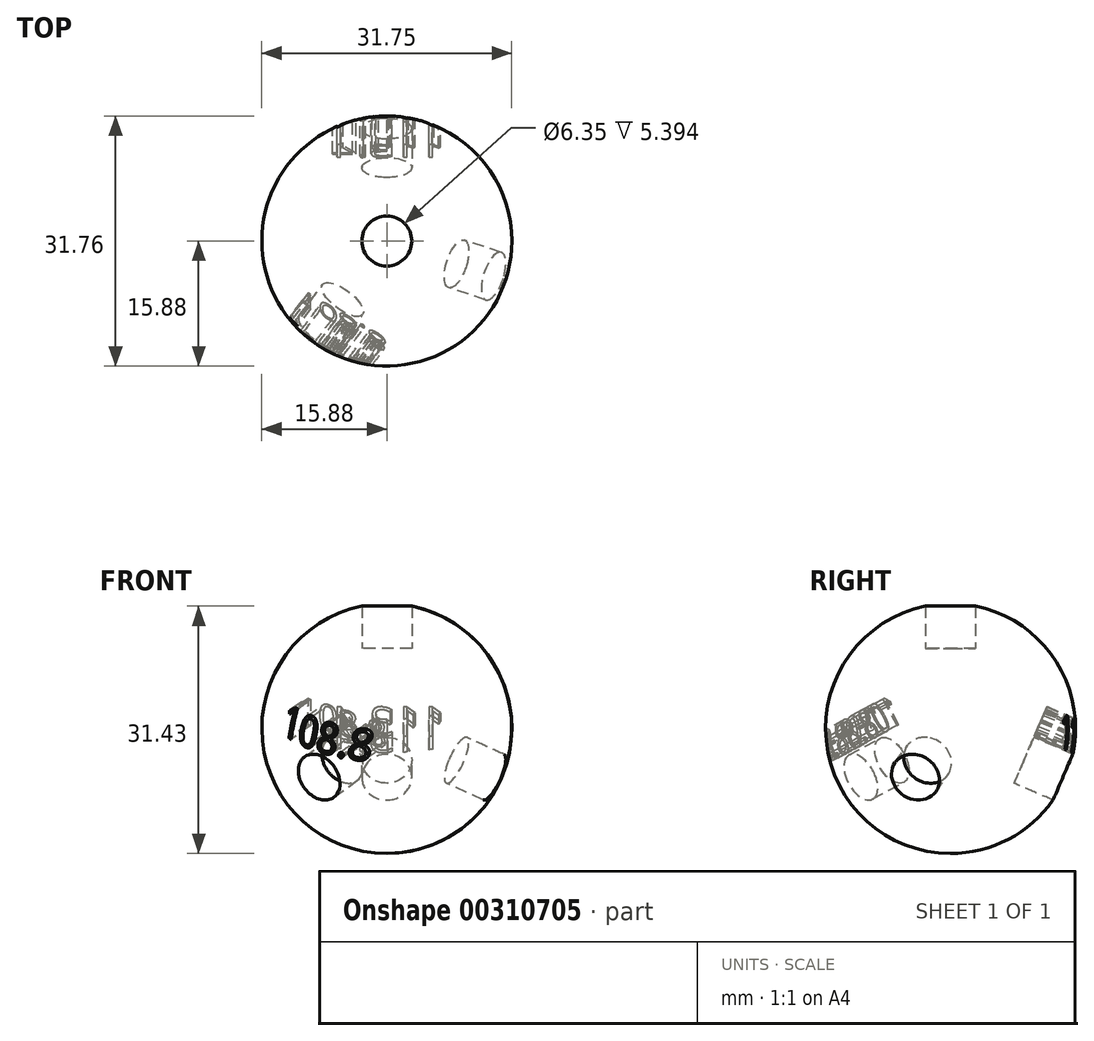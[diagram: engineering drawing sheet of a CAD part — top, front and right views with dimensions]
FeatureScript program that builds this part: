
annotation { "Feature Type Name" : "Feature", "Feature Type Description" : "" }
export const myFeature = defineFeature(function(context is Context, id is Id, definition is map)
    precondition{}
    {
        {
            var Q0;
            Q0=qCreatedBy(makeId("Front.planeOp"),FACE);
            var sketch = newSketch(context, id + "F0", { "sketchPlane" : qUnion([Q0])});
            skArc(sketch, "E0", {"start": v(0, 15.88) * mm, "mid": v(-15.88, 0) * mm, "end": v(0, -15.88) * mm});
            skLineSegment(sketch, "E1", {"start": v(0, 15.88) * mm, "end": v(0, -15.88) * mm});
            skSolve(sketch);
        }
        {
            var Q0;
            Q0=qCreatedBy(makeId("Top.planeOp"),FACE);
            var sketch = newSketch(context, id + "F1", { "sketchPlane" : qUnion([Q0])});
            skCircle(sketch, "E2", {"center": v(0, 0) * mm, "radius": 15.88 * mm});
            skSolve(sketch);
        }
        {
            var Q0;
            Q0=makeQuery(id+"F0.imprint","IMPRINT",FACE,{"disambiguationData":[TD([[makeQuery(id+"F0.imprint","IMPRINT",EDGE,{"derivedFrom":sQuery(id+"F0.wireOp",EDGE,"E0")}),1.0]])]});
            var Q1;
            Q1=sQuery(id+"F1.wireOp",EDGE,"E2");
            revolve(context, id + "F2", {"entities" : qUnion([Q0]), "axis" : qUnion([Q1]), "revolveType" : RevolveType.FULL});
        }
        {
            var Q0;
            Q0=qCreatedBy(makeId("Top.planeOp"),FACE);
            cPlane(context, id + "F3", {"entities" : qUnion([Q0]), "cplaneType" : CPlaneType.OFFSET, "offset" : 10.16 * mm, "width" : 152.4 * mm, "height" : 152.4 * mm});
        }
        {
            var Q0;
            Q0=qCreatedBy(id+"F3.planeOp",FACE);
            var sketch = newSketch(context, id + "F4", { "sketchPlane" : qUnion([Q0])});
            skCircle(sketch, "E3", {"center": v(0, 0) * mm, "radius": 3.18 * mm});
            skSolve(sketch);
        }
        {
            var Q0;
            Q0=qSketchRegion(id+"F4",true);
            extrude(context, id + "F5", {"entities" : qUnion([Q0]), "depth" : 50.8 * mm});
        }
        {
            var Q0;
            Q0=qCreatedBy(makeId("Front.planeOp"),FACE);
            var sketch = newSketch(context, id + "F6", { "sketchPlane" : qUnion([Q0])});
            skLineSegment(sketch, "E4", {"start": v(0, 0) * mm, "end": v(0, -58.07) * mm, "construction": true});
            skLineSegment(sketch, "E5", {"start": v(0, 0) * mm, "end": v(-72.63, 0) * mm, "construction": true});
            skSolve(sketch);
        }
        {
            var Q0;
            Q0=makeQuery(id+"F5.opExtrude","SWEPT_BODY",BODY,{"disambiguationData":[OSD([sQuery(id+"F4.wireOp",EDGE,"E3")])]});
            var Q1;
            Q1=sQuery(id+"F6.wireOp",EDGE,"E5");
            transform(context, id + "F7", {"entities" : qUnion([Q0]), "transformType" : TransformType.ROTATION, "transformAxis" : qUnion([Q1]), "angle" : 113.4 * degree, "makeCopy" : true});
        }
        {
            var Q0;
            Q0=makeQuery(id+"F7.opPattern","COPY",BODY,{"derivedFrom":makeQuery(id+"F5.opExtrude","SWEPT_BODY",BODY,{"disambiguationData":[OSD([sQuery(id+"F4.wireOp",EDGE,"E3")])]}),"instanceName":"1"});
            var Q1;
            Q1=sQuery(id+"F6.wireOp",EDGE,"E4");
            transform(context, id + "F8", {"entities" : qUnion([Q0]), "transformType" : TransformType.ROTATION, "transformAxis" : qUnion([Q1]), "angle" : 108.2 * degree, "makeCopy" : true});
        }
        {
            var Q0;
            Q0=makeQuery(id+"F8.opPattern","COPY",BODY,{"derivedFrom":makeQuery(id+"F7.opPattern","COPY",BODY,{"derivedFrom":makeQuery(id+"F5.opExtrude","SWEPT_BODY",BODY,{"disambiguationData":[OSD([sQuery(id+"F4.wireOp",EDGE,"E3")])]}),"instanceName":"1"}),"instanceName":"1"});
            var Q1;
            Q1=sQuery(id+"F6.wireOp",EDGE,"E4");
            transform(context, id + "F9", {"entities" : qUnion([Q0]), "transformType" : TransformType.ROTATION, "transformAxis" : qUnion([Q1]), "angle" : 108.8 * degree, "makeCopy" : true});
        }
        {
            var Q0;
            Q0=makeQuery(id+"F7.opPattern","COPY",FACE,{"derivedFrom":makeQuery(id+"F5.opExtrude","CAP_FACE",FACE,{"disambiguationData":[OSD([sQuery(id+"F4.wireOp",EDGE,"E3")])],"isStart":false}),"instanceName":"1"});
            cPlane(context, id + "F10", {"entities" : qUnion([Q0]), "cplaneType" : CPlaneType.OFFSET, "offset" : 25.4 * mm, "oppositeDirection" : true, "width" : 152.4 * mm, "height" : 152.4 * mm});
        }
        {
            var Q0;
            Q0=qCreatedBy(id+"F10.planeOp",FACE);
            var sketch = newSketch(context, id + "F11", { "sketchPlane" : qUnion([Q0])});
            skText(sketch, "E6", { "text": "113.4", "fontName": "OpenSans-Regular.ttf"});
            const initialGuessF11  = {"E6": [-0.00732, 0.00336, 1, 0, 0.00404]};
            skSetInitialGuess(sketch, initialGuessF11);
            skSolve(sketch);
        }
        {
            var Q0;
            Q0 = qSketchRegion(id + "F11", true);
            extrude(context, id + "F12", {"entities" : qUnion([Q0]), "operationType" : NewBodyOperationType.REMOVE, "oppositeDirection" : true, "depth" : 25.4 * mm});
        }
        {
            var Q0;
            Q0=makeQuery(id+"F9.opPattern","COPY",FACE,{"derivedFrom":makeQuery(id+"F8.opPattern","COPY",FACE,{"derivedFrom":makeQuery(id+"F7.opPattern","COPY",FACE,{"derivedFrom":makeQuery(id+"F5.opExtrude","CAP_FACE",FACE,{"disambiguationData":[OSD([sQuery(id+"F4.wireOp",EDGE,"E3")])],"isStart":false}),"instanceName":"1"}),"instanceName":"1"}),"instanceName":"1"});
            cPlane(context, id + "F13", {"entities" : qUnion([Q0]), "cplaneType" : CPlaneType.OFFSET, "offset" : 25.4 * mm, "oppositeDirection" : true, "width" : 152.4 * mm, "height" : 152.4 * mm});
        }
        {
            var Q0;
            Q0=qCreatedBy(id+"F13.planeOp",FACE);
            var sketch = newSketch(context, id + "F14", { "sketchPlane" : qUnion([Q0])});
            skText(sketch, "E7", { "text": "108.8\n", "fontName": "OpenSans-Regular.ttf"});
            const initialGuessF14  = {"E7": [-0.0067, 0.0036, 1, 0, 0.00379]};
            skSetInitialGuess(sketch, initialGuessF14);
            skSolve(sketch);
        }
        {
            var Q0;
            Q0 = qSketchRegion(id + "F14", true);
            extrude(context, id + "F15", {"entities" : qUnion([Q0]), "operationType" : NewBodyOperationType.REMOVE, "oppositeDirection" : true, "depth" : 25.4 * mm});
        }
        {
            var Q0;
            Q0=makeQuery(id+"F5.opExtrude","SWEPT_BODY",BODY,{"disambiguationData":[OSD([sQuery(id+"F4.wireOp",EDGE,"E3")])]});
            var Q1;
            Q1=makeQuery(id+"F7.opPattern","COPY",BODY,{"derivedFrom":makeQuery(id+"F5.opExtrude","SWEPT_BODY",BODY,{"disambiguationData":[OSD([sQuery(id+"F4.wireOp",EDGE,"E3")])]}),"instanceName":"1"});
            var Q2;
            Q2=makeQuery(id+"F9.opPattern","COPY",BODY,{"derivedFrom":makeQuery(id+"F8.opPattern","COPY",BODY,{"derivedFrom":makeQuery(id+"F7.opPattern","COPY",BODY,{"derivedFrom":makeQuery(id+"F5.opExtrude","SWEPT_BODY",BODY,{"disambiguationData":[OSD([sQuery(id+"F4.wireOp",EDGE,"E3")])]}),"instanceName":"1"}),"instanceName":"1"}),"instanceName":"1"});
            var Q3;
            Q3=makeQuery(id+"F8.opPattern","COPY",BODY,{"derivedFrom":makeQuery(id+"F7.opPattern","COPY",BODY,{"derivedFrom":makeQuery(id+"F5.opExtrude","SWEPT_BODY",BODY,{"disambiguationData":[OSD([sQuery(id+"F4.wireOp",EDGE,"E3")])]}),"instanceName":"1"}),"instanceName":"1"});
            var Q4;
            Q4=makeQuery(id+"F2.opRevolve","SWEPT_BODY",BODY,{"disambiguationData":[OSD([sQuery(id+"F0.wireOp",EDGE,"E0"),sQuery(id+"F0.wireOp",EDGE,"E1")])]});
            booleanBodies(context, id + "F16", {"operationType" : BooleanOperationType.SUBTRACTION, "tools" : qUnion([Q0, Q1, Q2, Q3]), "targets" : qUnion([Q4])});
        }
    });
